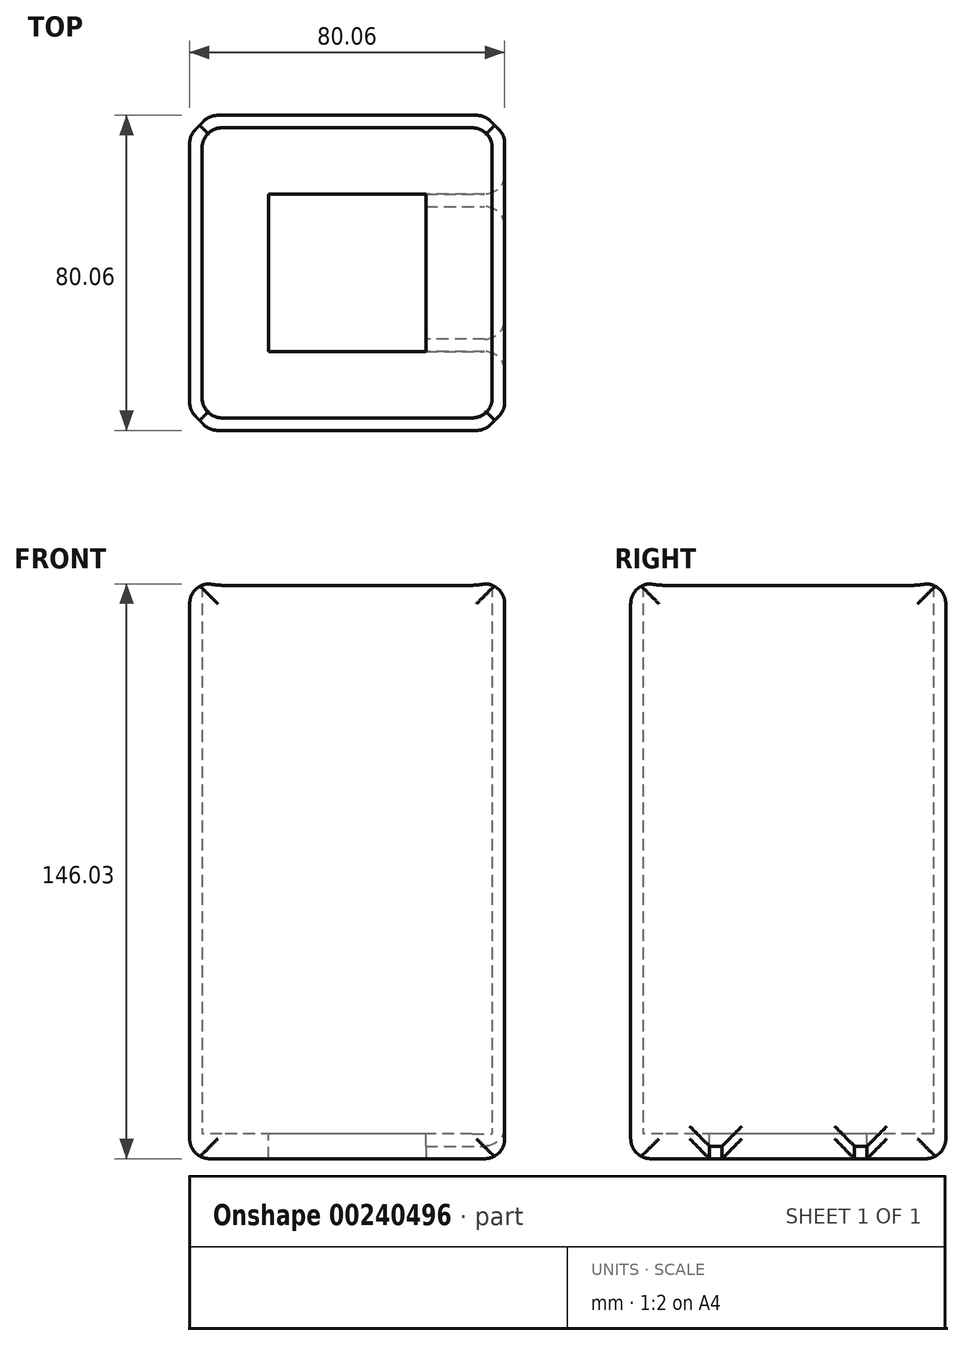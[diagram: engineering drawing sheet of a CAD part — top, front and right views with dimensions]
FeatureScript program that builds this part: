
annotation { "Feature Type Name" : "Feature", "Feature Type Description" : "" }
export const myFeature = defineFeature(function(context is Context, id is Id, definition is map)
    precondition{}
    {
        {
            var Q0;
            Q0=qCreatedBy(makeId("Top.planeOp"),FACE);
            var sketch = newSketch(context, id + "F0", { "sketchPlane" : qUnion([Q0])});
            skLineSegment(sketch, "E0.bottom", {"start": v(20, 20) * mm, "end": v(-20, 20) * mm});
            skLineSegment(sketch, "E0.top", {"start": v(20, -20) * mm, "end": v(-20, -20) * mm});
            skLineSegment(sketch, "E0.left", {"start": v(20, 20) * mm, "end": v(20, -20) * mm});
            skLineSegment(sketch, "E0.right", {"start": v(-20, 20) * mm, "end": v(-20, -20) * mm});
            skPoint(sketch, "E0.middle", {"position": v(0, 0) * mm});
            skLineSegment(sketch, "E1.bottom", {"start": v(36.85, 36.85) * mm, "end": v(-36.85, 36.85) * mm});
            skLineSegment(sketch, "E1.top", {"start": v(36.85, -36.85) * mm, "end": v(-36.85, -36.85) * mm});
            skLineSegment(sketch, "E1.left", {"start": v(36.85, 36.85) * mm, "end": v(36.85, -36.85) * mm});
            skLineSegment(sketch, "E1.right", {"start": v(-36.85, 36.85) * mm, "end": v(-36.85, -36.85) * mm});
            skLineSegment(sketch, "E2.bottom", {"start": v(-40.03, 40.03) * mm, "end": v(40.03, 40.03) * mm});
            skLineSegment(sketch, "E2.top", {"start": v(-40.03, -40.03) * mm, "end": v(40.03, -40.03) * mm});
            skLineSegment(sketch, "E2.left", {"start": v(-40.03, 40.03) * mm, "end": v(-40.03, -40.03) * mm});
            skLineSegment(sketch, "E2.right", {"start": v(40.03, 40.03) * mm, "end": v(40.03, -40.03) * mm});
            skSolve(sketch);
        }
        {
            var Q0;
            Q0=makeQuery(id+"F0.imprint","IMPRINT",FACE,{"disambiguationData":[TD([[makeQuery(id+"F0.imprint","IMPRINT",EDGE,{"derivedFrom":sQuery(id+"F0.wireOp",EDGE,"E0.bottom")}),-1.0]])]});
            var Q1;
            Q1=makeQuery(id+"F0.imprint","IMPRINT",FACE,{"disambiguationData":[TD([[makeQuery(id+"F0.imprint","IMPRINT",EDGE,{"derivedFrom":sQuery(id+"F0.wireOp",EDGE,"E0.bottom")}),1.0]])]});
            var Q2;
            Q2=makeQuery(id+"F0.imprint","IMPRINT",FACE,{"disambiguationData":[TD([[makeQuery(id+"F0.imprint","IMPRINT",EDGE,{"derivedFrom":sQuery(id+"F0.wireOp",EDGE,"E1.bottom")}),-1.0]])]});
            extrude(context, id + "F1", {"entities" : qUnion([Q0, Q1, Q2]), "oppositeDirection" : true, "depth" : 6.35 * mm});
        }
        {
            var Q0;
            Q0=makeQuery(id+"F0.imprint","IMPRINT",FACE,{"disambiguationData":[TD([[makeQuery(id+"F0.imprint","IMPRINT",EDGE,{"derivedFrom":sQuery(id+"F0.wireOp",EDGE,"E0.bottom")}),1.0]])]});
            extrude(context, id + "F2", {"entities" : qUnion([Q0]), "operationType" : NewBodyOperationType.REMOVE, "oppositeDirection" : true, "depth" : 9.14 * mm});
        }
        {
            var Q0;
            Q0=makeQuery(id+"F0.imprint","IMPRINT",FACE,{"disambiguationData":[TD([[makeQuery(id+"F0.imprint","IMPRINT",EDGE,{"derivedFrom":sQuery(id+"F0.wireOp",EDGE,"E1.bottom")}),-1.0]])]});
            extrude(context, id + "F3", {"entities" : qUnion([Q0]), "operationType" : NewBodyOperationType.ADD, "depth" : 139.7 * mm});
        }
        {
            var Q0;
            Q0=makeQuery(id+"F1.opExtrude","CAP_FACE",FACE,{"disambiguationData":[OSD([sQuery(id+"F0.wireOp",EDGE,"E2.bottom"),sQuery(id+"F0.wireOp",EDGE,"E2.top"),sQuery(id+"F0.wireOp",EDGE,"E2.left"),sQuery(id+"F0.wireOp",EDGE,"E2.right")])],"isStart":false});
            var sketch = newSketch(context, id + "F4", { "sketchPlane" : qUnion([Q0])});
            skLineSegment(sketch, "E3", {"start": v(20, 20) * mm, "end": v(40.03, 20) * mm});
            skLineSegment(sketch, "E4", {"start": v(40.03, 16.82) * mm, "end": v(20, 16.82) * mm});
            skLineSegment(sketch, "E5", {"start": v(20, -20) * mm, "end": v(40.03, -20) * mm});
            skLineSegment(sketch, "E6", {"start": v(20, -16.82) * mm, "end": v(40.03, -16.82) * mm});
            skSolve(sketch);
        }
        {
            var Q0;
            {var subQ0=sQuery(id+"F4.wireOp",EDGE,"E3");Q0=makeQuery(id+"F4.imprint","IMPRINT",FACE,{"disambiguationData":[TD([[makeQuery(id+"F4.imprint","IMPRINT",EDGE,{"derivedFrom":subQ0}),-1.0]])]});}
            var Q1;
            {var subQ0=sQuery(id+"F4.wireOp",EDGE,"E5");Q1=makeQuery(id+"F4.imprint","IMPRINT",FACE,{"disambiguationData":[TD([[makeQuery(id+"F4.imprint","IMPRINT",EDGE,{"derivedFrom":subQ0}),1.0]])]});}
            extrude(context, id + "F5", {"entities" : qUnion([Q0, Q1]), "operationType" : NewBodyOperationType.REMOVE, "oppositeDirection" : true, "depth" : 3.17 * mm});
        }
        {
            var Q0;
            {var subQ0=sQuery(id+"F0.wireOp",EDGE,"E2.right");var subQ1=sQuery(id+"F0.wireOp",EDGE,"E2.top");Q0=makeQuery(id+"F3.boolean.opBoolean","MERGE",EDGE,{"derivedFrom":[makeQuery(id+"F1.opExtrude","SWEPT_EDGE",EDGE,{"disambiguationData":[OSD([subQ1,subQ0])]}),makeQuery(id+"F3.opExtrude","SWEPT_EDGE",EDGE,{"disambiguationData":[OSD([subQ1,subQ0])]})]});}
            var Q1;
            {var subQ0=sQuery(id+"F0.wireOp",EDGE,"E2.left");var subQ1=sQuery(id+"F0.wireOp",EDGE,"E2.top");Q1=makeQuery(id+"F3.boolean.opBoolean","MERGE",EDGE,{"derivedFrom":[makeQuery(id+"F1.opExtrude","SWEPT_EDGE",EDGE,{"disambiguationData":[OSD([subQ1,subQ0])]}),makeQuery(id+"F3.opExtrude","SWEPT_EDGE",EDGE,{"disambiguationData":[OSD([subQ1,subQ0])]})]});}
            var Q2;
            {var subQ0=sQuery(id+"F0.wireOp",EDGE,"E2.left");var subQ1=sQuery(id+"F0.wireOp",EDGE,"E2.bottom");Q2=makeQuery(id+"F3.boolean.opBoolean","MERGE",EDGE,{"derivedFrom":[makeQuery(id+"F1.opExtrude","SWEPT_EDGE",EDGE,{"disambiguationData":[OSD([subQ1,subQ0])]}),makeQuery(id+"F3.opExtrude","SWEPT_EDGE",EDGE,{"disambiguationData":[OSD([subQ1,subQ0])]})]});}
            var Q3;
            {var subQ0=sQuery(id+"F0.wireOp",EDGE,"E2.right");var subQ1=sQuery(id+"F0.wireOp",EDGE,"E2.bottom");Q3=makeQuery(id+"F3.boolean.opBoolean","MERGE",EDGE,{"derivedFrom":[makeQuery(id+"F1.opExtrude","SWEPT_EDGE",EDGE,{"disambiguationData":[OSD([subQ1,subQ0])]}),makeQuery(id+"F3.opExtrude","SWEPT_EDGE",EDGE,{"disambiguationData":[OSD([subQ1,subQ0])]})]});}
            chamfer(context, id + "F6", {"entities" : qUnion([Q0, Q1, Q2, Q3]), "width" : 5.08 * mm, "tangentPropagation" : true});
        }
        {
            var Q0;
            {var subQ0=sQuery(id+"F0.wireOp",EDGE,"E2.left");Q0=makeQuery(id+"F3.boolean.opBoolean","MERGE",FACE,{"derivedFrom":[makeQuery(id+"F1.opExtrude","SWEPT_FACE",FACE,{"disambiguationData":[OSD([subQ0])]}),makeQuery(id+"F3.opExtrude","SWEPT_FACE",FACE,{"disambiguationData":[OSD([subQ0])]})]});}
            var Q1;
            {var subQ0=sQuery(id+"F0.wireOp",EDGE,"E2.bottom");Q1=makeQuery(id+"F3.boolean.opBoolean","MERGE",FACE,{"derivedFrom":[makeQuery(id+"F1.opExtrude","SWEPT_FACE",FACE,{"disambiguationData":[OSD([subQ0])]}),makeQuery(id+"F3.opExtrude","SWEPT_FACE",FACE,{"disambiguationData":[OSD([subQ0])]})]});}
            var Q2;
            {var subQ0=sQuery(id+"F0.wireOp",EDGE,"E2.right");Q2=makeQuery(id+"F3.boolean.opBoolean","MERGE",FACE,{"derivedFrom":[makeQuery(id+"F1.opExtrude","SWEPT_FACE",FACE,{"disambiguationData":[OSD([subQ0])]}),makeQuery(id+"F3.opExtrude","SWEPT_FACE",FACE,{"disambiguationData":[OSD([subQ0])]})]});}
            var Q3;
            {var subQ0=sQuery(id+"F0.wireOp",EDGE,"E2.top");Q3=makeQuery(id+"F3.boolean.opBoolean","MERGE",FACE,{"derivedFrom":[makeQuery(id+"F1.opExtrude","SWEPT_FACE",FACE,{"disambiguationData":[OSD([subQ0])]}),makeQuery(id+"F3.opExtrude","SWEPT_FACE",FACE,{"disambiguationData":[OSD([subQ0])]})]});}
            fillet(context, id + "F7", {"entities" : qUnion([Q0, Q1, Q2, Q3]), "radius" : 5.08 * mm, "tangentPropagation" : true, "allowEdgeOverflow" : false});
        }
        {
            var Q0;
            Q0=makeQuery(id+"F3.opExtrude","SWEPT_EDGE",EDGE,{"disambiguationData":[OSD([sQuery(id+"F0.wireOp",EDGE,"E1.bottom"),sQuery(id+"F0.wireOp",EDGE,"E1.left")])]});
            var Q1;
            Q1=makeQuery(id+"F3.opExtrude","SWEPT_EDGE",EDGE,{"disambiguationData":[OSD([sQuery(id+"F0.wireOp",EDGE,"E1.top"),sQuery(id+"F0.wireOp",EDGE,"E1.left")])]});
            var Q2;
            Q2=makeQuery(id+"F3.opExtrude","SWEPT_EDGE",EDGE,{"disambiguationData":[OSD([sQuery(id+"F0.wireOp",EDGE,"E1.top"),sQuery(id+"F0.wireOp",EDGE,"E1.right")])]});
            var Q3;
            Q3=makeQuery(id+"F3.opExtrude","SWEPT_EDGE",EDGE,{"disambiguationData":[OSD([sQuery(id+"F0.wireOp",EDGE,"E1.bottom"),sQuery(id+"F0.wireOp",EDGE,"E1.right")])]});
            fillet(context, id + "F8", {"entities" : qUnion([Q0, Q1, Q2, Q3]), "radius" : 5.08 * mm, "tangentPropagation" : true, "allowEdgeOverflow" : false});
        }
    });
